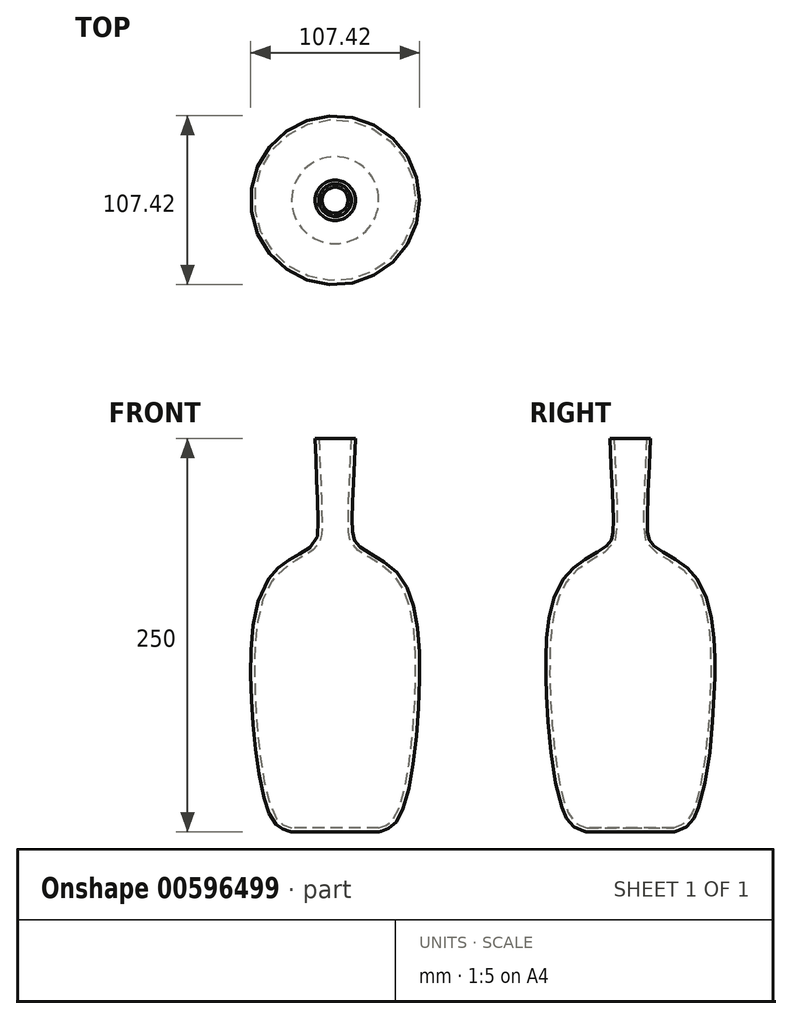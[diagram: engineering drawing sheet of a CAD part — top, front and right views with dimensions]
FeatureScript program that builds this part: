
annotation { "Feature Type Name" : "Feature", "Feature Type Description" : "" }
export const myFeature = defineFeature(function(context is Context, id is Id, definition is map)
    precondition{}
    {
        {
            var Q0;
            Q0=qCreatedBy(makeId("Front.planeOp"),FACE);
            var sketch = newSketch(context, id + "F0", { "sketchPlane" : qUnion([Q0])});
            skLineSegment(sketch, "E0", {"start": v(0, -213.74) * mm, "end": v(28.21, -213.74) * mm});
            skFitSpline(sketch, "E1", {"points": [v(28.21, -213.74) * mm, v(38.14, -208.44) * mm, v(53.26, -127.57) * mm, v(40.67, -50.78) * mm, v(14.59, -31.84) * mm, v(10.81, -20.07) * mm, v(12.84, 36.26) * mm], "startDerivative": vector(87.14, 44.55) * mm, "endDerivative": vector(12.59, 332.87) * mm});
            skLineSegment(sketch, "E2", {"start": v(12.84, 36.26) * mm, "end": v(0, 36.26) * mm});
            skLineSegment(sketch, "E3", {"start": v(0, 36.26) * mm, "end": v(0, -213.74) * mm});
            skSolve(sketch);
        }
        {
            var Q0;
            Q0 = qSketchRegion(id + "F0", true);
            var Q1;
            Q1=sQuery(id+"F0.wireOp",EDGE,"E3");
            revolve(context, id + "F1", {"entities" : qUnion([Q0]), "axis" : qUnion([Q1]), "revolveType" : RevolveType.FULL});
        }
        {
            var Q0;
            Q0=makeQuery(id+"F1.opRevolve","SWEPT_FACE",FACE,{"disambiguationData":[OSD([sQuery(id+"F0.wireOp",EDGE,"E2")])]});
            shell(context, id + "F2", {"entities" : qUnion([Q0]), "thickness" : 2.5 * mm});
        }
        {
            var Q0;
            Q0=makeQuery(id+"F1.opRevolve","SWEPT_EDGE",EDGE,{"disambiguationData":[OSD([sQuery(id+"F0.wireOp",EDGE,"E0"),sQuery(id+"F0.wireOp",EDGE,"E1")])]});
            fillet(context, id + "F3", {"entities" : qUnion([Q0]), "radius" : 5 * mm, "tangentPropagation" : true, "allowEdgeOverflow" : false});
        }
    });
